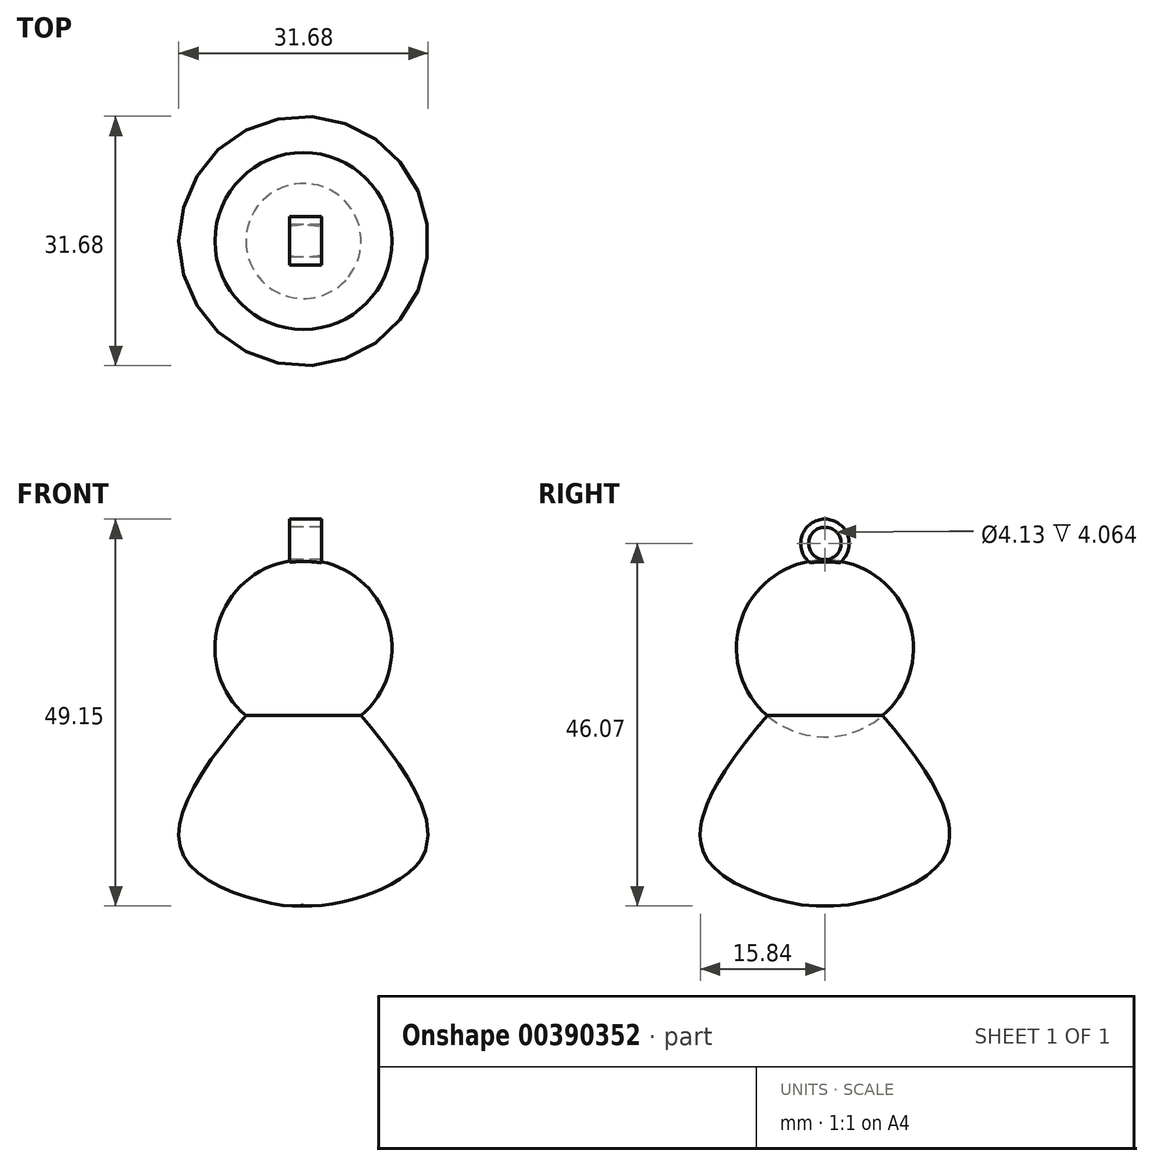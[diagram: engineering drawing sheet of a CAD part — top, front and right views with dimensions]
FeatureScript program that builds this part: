
annotation { "Feature Type Name" : "Feature", "Feature Type Description" : "" }
export const myFeature = defineFeature(function(context is Context, id is Id, definition is map)
    precondition{}
    {
        {
            var Q0;
            Q0=qCreatedBy(makeId("Front.planeOp"),FACE);
            var sketch = newSketch(context, id + "F0", { "sketchPlane" : qUnion([Q0])});
            skLineSegment(sketch, "E0", {"start": v(0, 25.1) * mm, "end": v(0, -15.6) * mm});
            skFitSpline(sketch, "E1", {"points": [v(0, 25.1) * mm, v(-14.77, -1.56) * mm, v(0, -7.05) * mm, v(0, -6.24) * mm], "startDerivative": vector(-53.94, -58.5) * mm, "endDerivative": vector(-5.32, 11.02) * mm});
            skSolve(sketch);
        }
        {
            var Q0;
            Q0=qCreatedBy(makeId("Top.planeOp"),FACE);
            var sketch = newSketch(context, id + "F1", { "sketchPlane" : qUnion([Q0])});
            skCircle(sketch, "E2", {"center": v(0, 0) * mm, "radius": 15.55 * mm});
            skSolve(sketch);
        }
        {
            var Q0;
            {var subQ0=sQuery(id+"F0.wireOp",EDGE,"E1");var subQ1=sQuery(id+"F0.wireOp",EDGE,"E0");var subQ2=makeQuery(id+"F0.imprint","INTERSECT",VERTEX,{"disambiguationData":[OD(0.0)],"derivedFrom":[subQ1,subQ0]});Q0=makeQuery(id+"F0.imprint","IMPRINT",FACE,{"disambiguationData":[TD([[makeQuery(id+"F0.imprint","IMPRINT",EDGE,{"disambiguationData":[TD([[subQ2,-1.0]])],"derivedFrom":subQ1}),-1.0]])]});}
            var Q1;
            Q1=sQuery(id+"F1.wireOp",EDGE,"E2");
            revolve(context, id + "F2", {"entities" : qUnion([Q0]), "axis" : qUnion([Q1]), "revolveType" : RevolveType.FULL});
        }
        {
            var Q0;
            Q0=qCreatedBy(makeId("Top.planeOp"),FACE);
            cPlane(context, id + "F3", {"entities" : qUnion([Q0]), "cplaneType" : CPlaneType.OFFSET, "offset" : 25.4 * mm, "width" : 152.4 * mm, "height" : 152.4 * mm});
        }
        {
            var Q0;
            Q0=qCreatedBy(makeId("Front.planeOp"),FACE);
            var sketch = newSketch(context, id + "F4", { "sketchPlane" : qUnion([Q0])});
            skArc(sketch, "E3", {"start": v(0, 36.77) * mm, "mid": v(-11.25, 25.52) * mm, "end": v(0, 14.28) * mm});
            skLineSegment(sketch, "E4", {"start": v(0, 36.77) * mm, "end": v(0, 14.28) * mm});
            skSolve(sketch);
        }
        {
            var Q0;
            Q0=qCreatedBy(id+"F3.planeOp",FACE);
            var sketch = newSketch(context, id + "F5", { "sketchPlane" : qUnion([Q0])});
            skCircle(sketch, "E5", {"center": v(0, 0) * mm, "radius": 9.04 * mm});
            skSolve(sketch);
        }
        {
            var Q0;
            Q0=makeQuery(id+"F4.imprint","IMPRINT",FACE,{"disambiguationData":[TD([[makeQuery(id+"F4.imprint","IMPRINT",EDGE,{"derivedFrom":sQuery(id+"F4.wireOp",EDGE,"E3")}),1.0]])]});
            var Q1;
            Q1=sQuery(id+"F5.wireOp",EDGE,"E5");
            revolve(context, id + "F6", {"operationType" : NewBodyOperationType.ADD, "entities" : qUnion([Q0]), "axis" : qUnion([Q1]), "revolveType" : RevolveType.FULL});
        }
        {
            var Q0;
            Q0=qCreatedBy(makeId("Right.planeOp"),FACE);
            var sketch = newSketch(context, id + "F7", { "sketchPlane" : qUnion([Q0])});
            skCircle(sketch, "E6", {"center": v(0, 38.86) * mm, "radius": 3.08 * mm});
            skSolve(sketch);
        }
        {
            var Q0;
            Q0=makeQuery(id+"F7.imprint","IMPRINT",FACE,{"disambiguationData":[TD([[makeQuery(id+"F7.imprint","IMPRINT",EDGE,{"derivedFrom":sQuery(id+"F7.wireOp",EDGE,"E6")}),1.0]])]});
            extrude(context, id + "F8", {"entities" : qUnion([Q0]), "operationType" : NewBodyOperationType.ADD, "oppositeDirection" : true, "depth" : 1.78 * mm, "hasSecondDirection" : true, "secondDirectionOppositeDirection" : false, "secondDirectionDepth" : 2.3 * mm});
        }
        {
            var Q0;
            Q0=makeQuery(id+"F8.opExtrude","CAP_FACE",FACE,{"disambiguationData":[OSD([sQuery(id+"F7.wireOp",EDGE,"E6")])],"isStart":false});
            var sketch = newSketch(context, id + "F9", { "sketchPlane" : qUnion([Q0])});
            skCircle(sketch, "E7", {"center": v(0, 38.86) * mm, "radius": 2.06 * mm});
            skSolve(sketch);
        }
        {
            var Q0;
            Q0=makeQuery(id+"F9.imprint","IMPRINT",FACE,{"disambiguationData":[TD([[makeQuery(id+"F9.imprint","IMPRINT",EDGE,{"derivedFrom":sQuery(id+"F9.wireOp",EDGE,"E7")}),1.0]])]});
            extrude(context, id + "F10", {"entities" : qUnion([Q0]), "operationType" : NewBodyOperationType.REMOVE, "oppositeDirection" : true, "depth" : 25.4 * mm});
        }
    });
